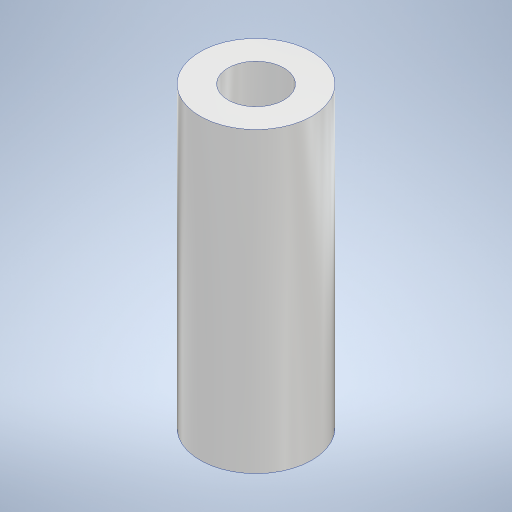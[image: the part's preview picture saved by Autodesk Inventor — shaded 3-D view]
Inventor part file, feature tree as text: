
AUTODESK INVENTOR PART (.ipt)
format: ipt  version: 2023 (Build 270158000, 158)  size: 223,744 bytes
history: native  units: mm
features: other x1, extrude x1, sketch x1
ambient origin geometry x8: Origin, YZ Plane, XZ Plane, XY Plane, X Axis, Y Axis, Z Axis, Center Point
bodies: Body1 (feature_tree)
feature tree (3):
  other  "ソリッド1"
  extrude  "押し出し1"  Depth=6.0mm
  sketch  "スケッチ1"
